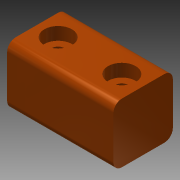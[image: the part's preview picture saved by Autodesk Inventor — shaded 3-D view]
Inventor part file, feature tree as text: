
AUTODESK INVENTOR PART (.ipt)
format: ipt  version: 2013 (Build 170138000, 138)  size: 104,960 bytes
history: native  units: mm
features: fillet x2, sketch x2, extrude x1, hole x1
ambient origin geometry x8: Origin, YZ Plane, XZ Plane, XY Plane, X Axis, Y Axis, Z Axis, Center Point
bodies: Solid1 (feature_tree)
feature tree (6):
  extrude  "Extrusion1"  Depth=14.0mm
  hole  "Hole1"  [1 undecoded]
  fillet  "Fillet1"  Radius=2.0mm
  fillet  "Fillet2"  Radius=2.0mm
  sketch  "Sketch1"  dims[d0=25.0mm d2=14.0mm]
  sketch  "Sketch2"  dims[d3=14.0mm d4=0.0mm d5=15.0mm d7=3.1mm d8=6.0mm d9=6.5mm d10=3.0mm d11=90.0deg d12=8.0mm d13=20.594885mm d14=2.0mm d15=2.0mm]
note: 1 required parameter value undecoded (feature->parameter linkage not recoverable at this tier; creation-order binding heuristic only, values carry confidence <= 0.55)
